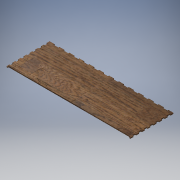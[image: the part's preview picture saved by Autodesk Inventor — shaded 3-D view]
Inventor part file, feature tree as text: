
AUTODESK INVENTOR PART (.ipt)
format: ipt  version: 2018.3 (Build 223284000, 284)  size: 1,110,528 bytes
history: native  units: mm
features: other x14, reference x10, extrude x5, sketch x5
ambient origin geometry x8: Origin, YZ Plane, XZ Plane, XY Plane, X Axis, Y Axis, Z Axis, Center Point
bodies: Solido1 (feature_tree)
feature tree (34):
  extrude  "Estrusione1"  Depth=467.0mm
  extrude  "Estrusione2"  Depth=157.0mm
  extrude  "Estrusione3"  Depth=4.0mm TaperAngle=0.0deg
  extrude  "Estrusione4"  Depth=4.0mm
  extrude  "Estrusione5"  Depth=475.0mm
  sketch  "Schizzo1"
  sketch  "Schizzo3"
  other  "Linea chiusa proiettata2"
  sketch  "Schizzo4"
  reference  "Riferimento1"
  reference  "Riferimento2"
  reference  "Riferimento3"
  reference  "Riferimento4"
  reference  "Riferimento5"
  reference  "Riferimento6"
  reference  "Riferimento7"
  sketch  "Schizzo5"
  reference  "Riferimento9"
  reference  "Riferimento11"
  reference  "Riferimento12"
  sketch  "Schizzo6"
  other  "<userpath>\Desktop\Scorbot Hardware\Case Board V2\caseHw v2.iam"
  other  "caseHw v2.iam"
  other  "matherBoard v1:1"
  other  "PCB Component:1"
  other  "Board:1"
  other  "Raspberry Pi 3:1"
  other  "Raspberry Pi 347_115"
  other  "Raspberry Pi 345_113"
  other  "Raspberry Pi 349_117"
  other  "Raspberry Pi 351_119"
  other  "Dietro:1"
  other  "LatoPy:1"
  other  "LatoAlimentatore:1"
